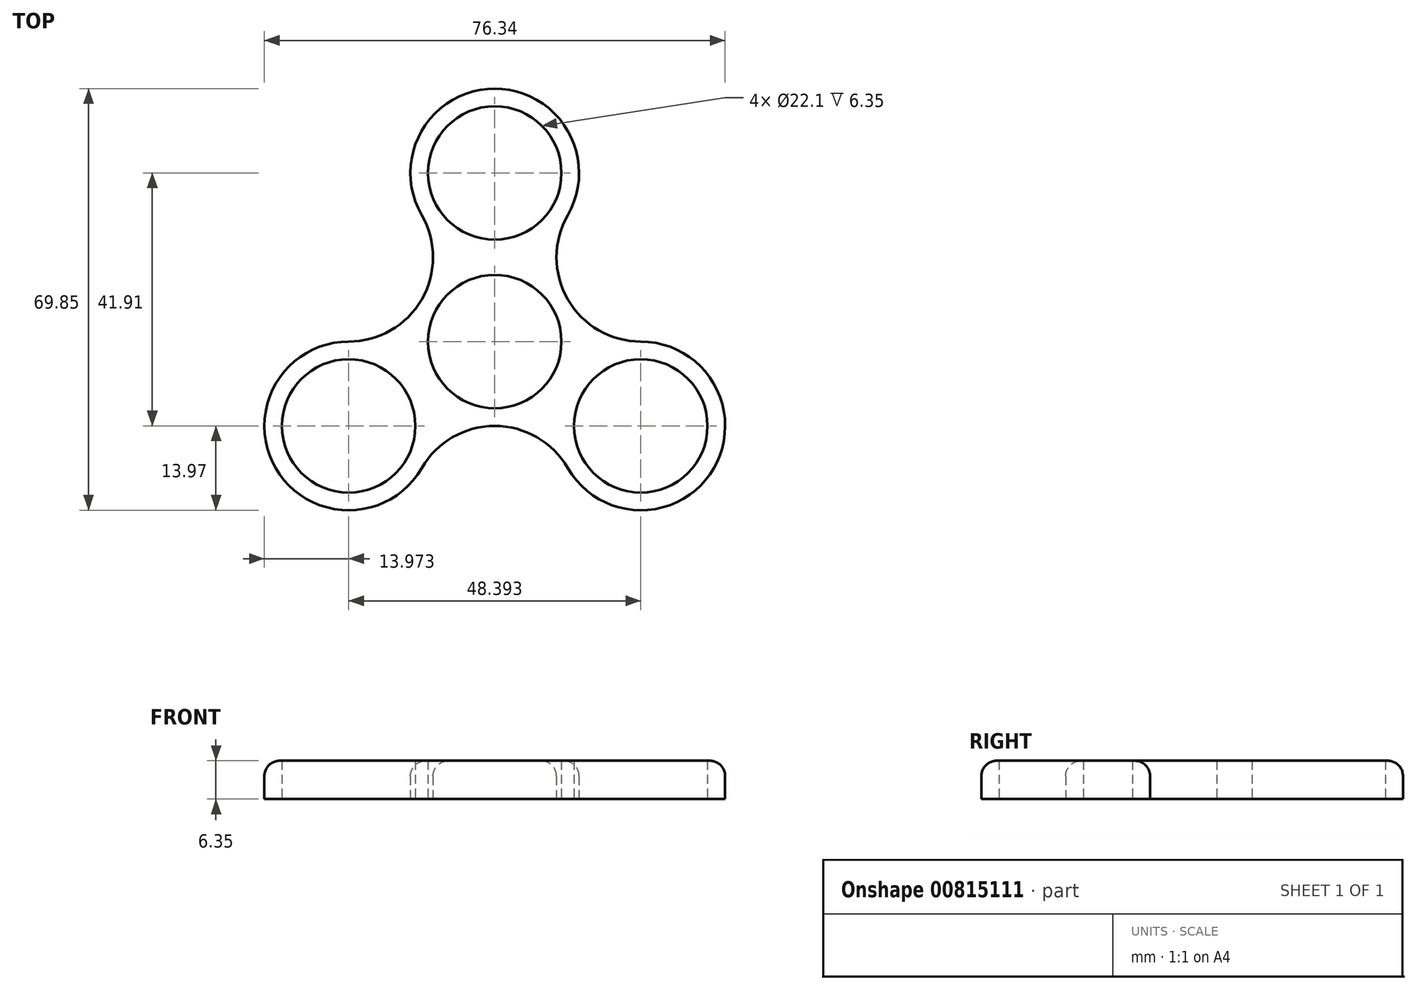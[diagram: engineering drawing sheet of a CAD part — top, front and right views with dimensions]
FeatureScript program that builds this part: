
annotation { "Feature Type Name" : "Feature", "Feature Type Description" : "" }
export const myFeature = defineFeature(function(context is Context, id is Id, definition is map)
    precondition{}
    {
        {
            var Q0;
            Q0=qCreatedBy(makeId("Top.planeOp"),FACE);
            var sketch = newSketch(context, id + "F0", { "sketchPlane" : qUnion([Q0])});
            skCircle(sketch, "E0", {"center": v(0, 0) * mm, "radius": 11.05 * mm});
            skLineSegment(sketch, "E1", {"start": v(0, 0) * mm, "end": v(0, 27.94) * mm});
            skCircle(sketch, "E2", {"center": v(0, 27.94) * mm, "radius": 11.05 * mm});
            skCircle(sketch, "E3", {"center": v(0, 27.94) * mm, "radius": 13.97 * mm});
            skCircle(sketch, "E4.1.0", {"center": v(-24.2, -13.97) * mm, "radius": 13.97 * mm});
            skCircle(sketch, "E4.1.1", {"center": v(-24.2, -13.97) * mm, "radius": 11.05 * mm});
            skCircle(sketch, "E4.2.0", {"center": v(24.2, -13.97) * mm, "radius": 13.97 * mm});
            skCircle(sketch, "E4.2.1", {"center": v(24.2, -13.97) * mm, "radius": 11.05 * mm});
            skLineSegment(sketch, "E5", {"start": v(0, 0) * mm, "end": v(-24.2, 13.97) * mm});
            skCircle(sketch, "E6", {"center": v(0, 0) * mm, "radius": 13.97 * mm});
            skArc(sketch, "E7", {"start": v(-24.2, 0) * mm, "mid": v(-12.1, 6.99) * mm, "end": v(-12.1, 20.96) * mm});
            skArc(sketch, "E8.1.0", {"start": v(12.1, -20.96) * mm, "mid": v(0, -13.97) * mm, "end": v(-12.1, -20.95) * mm});
            skArc(sketch, "E8.2.0", {"start": v(12.1, 20.95) * mm, "mid": v(12.1, 6.98) * mm, "end": v(24.2, 0) * mm});
            skSolve(sketch);
        }
        {
            var Q0;
            Q0 = qSketchRegion(id + "F0", true);
            extrude(context, id + "F1", {"entities" : qUnion([Q0]), "depth" : 6.35 * mm, "offsetDistance" : 25.4 * mm});
        }
        {
            var Q0;
            Q0=makeQuery(id+"F1.opExtrude","CAP_EDGE",EDGE,{"disambiguationData":[OSD([sQuery(id+"F0.wireOp",EDGE,"E8.1.0")])],"isStart":false});
            fillet(context, id + "F2", {"entities" : qUnion([Q0]), "radius" : 2.54 * mm, "tangentPropagation" : true, "allowEdgeOverflow" : false});
        }
    });
